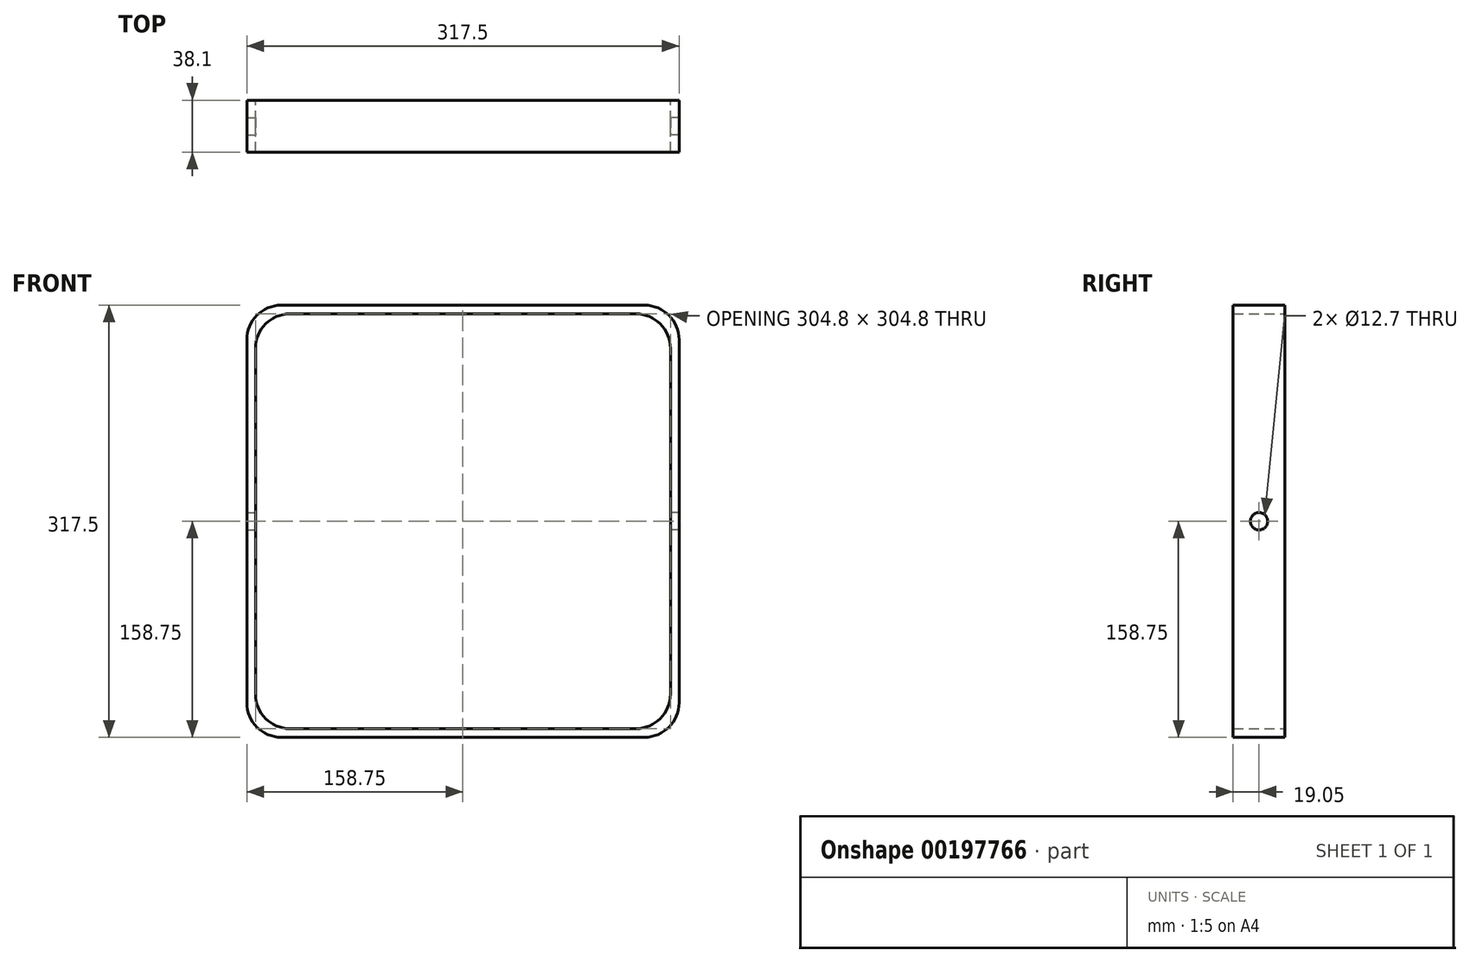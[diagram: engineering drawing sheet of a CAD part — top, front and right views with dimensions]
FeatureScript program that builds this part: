
annotation { "Feature Type Name" : "Feature", "Feature Type Description" : "" }
export const myFeature = defineFeature(function(context is Context, id is Id, definition is map)
    precondition{}
    {
        {
            var Q0;
            Q0=qCreatedBy(makeId("Front.planeOp"),FACE);
            var sketch = newSketch(context, id + "F0", { "sketchPlane" : qUnion([Q0])});
            skLineSegment(sketch, "E0.bottom", {"start": v(152.4, -152.4) * mm, "end": v(-152.4, -152.4) * mm});
            skLineSegment(sketch, "E0.top", {"start": v(152.4, 152.4) * mm, "end": v(-152.4, 152.4) * mm});
            skLineSegment(sketch, "E0.left", {"start": v(152.4, -152.4) * mm, "end": v(152.4, 152.4) * mm});
            skLineSegment(sketch, "E0.right", {"start": v(-152.4, -152.4) * mm, "end": v(-152.4, 152.4) * mm});
            skPoint(sketch, "E0.middle", {"position": v(0, 0) * mm});
            skPoint(sketch, "E1.top.start.orphan", {"position": v(50.8, 44.45) * mm});
            skPoint(sketch, "E1.right.end.orphan", {"position": v(-50.8, 44.45) * mm});
            skPoint(sketch, "E1.bottom.end.orphan", {"position": v(-50.8, -44.45) * mm});
            skPoint(sketch, "E1.bottom.start.orphan", {"position": v(50.8, -44.45) * mm});
            skLineSegment(sketch, "E2.bottom", {"start": v(158.75, -158.75) * mm, "end": v(-158.75, -158.75) * mm});
            skLineSegment(sketch, "E2.top", {"start": v(158.75, 158.75) * mm, "end": v(-158.75, 158.75) * mm});
            skLineSegment(sketch, "E2.left", {"start": v(158.75, -158.75) * mm, "end": v(158.75, 158.75) * mm});
            skLineSegment(sketch, "E2.right", {"start": v(-158.75, -158.75) * mm, "end": v(-158.75, 158.75) * mm});
            skSolve(sketch);
        }
        {
            var Q0;
            Q0=makeQuery(id+"F0.imprint","IMPRINT",FACE,{"disambiguationData":[TD([[makeQuery(id+"F0.imprint","IMPRINT",EDGE,{"derivedFrom":sQuery(id+"F0.wireOp",EDGE,"E0.bottom")}),1.0]])]});
            extrude(context, id + "F1", {"entities" : qUnion([Q0]), "depth" : 38.1 * mm});
        }
        {
            var Q0;
            Q0=makeQuery(id+"F1.opExtrude","SWEPT_EDGE",EDGE,{"disambiguationData":[OSD([sQuery(id+"F0.wireOp",EDGE,"E0.bottom"),sQuery(id+"F0.wireOp",EDGE,"E0.left")])]});
            var Q1;
            Q1=makeQuery(id+"F1.opExtrude","SWEPT_EDGE",EDGE,{"disambiguationData":[OSD([sQuery(id+"F0.wireOp",EDGE,"E0.bottom"),sQuery(id+"F0.wireOp",EDGE,"E0.right")])]});
            var Q2;
            Q2=makeQuery(id+"F1.opExtrude","SWEPT_EDGE",EDGE,{"disambiguationData":[OSD([sQuery(id+"F0.wireOp",EDGE,"E0.top"),sQuery(id+"F0.wireOp",EDGE,"E0.right")])]});
            var Q3;
            Q3=makeQuery(id+"F1.opExtrude","SWEPT_EDGE",EDGE,{"disambiguationData":[OSD([sQuery(id+"F0.wireOp",EDGE,"E0.top"),sQuery(id+"F0.wireOp",EDGE,"E0.left")])]});
            var Q4;
            Q4=makeQuery(id+"F1.opExtrude","SWEPT_EDGE",EDGE,{"disambiguationData":[OSD([sQuery(id+"F0.wireOp",EDGE,"E2.bottom"),sQuery(id+"F0.wireOp",EDGE,"E2.left")])]});
            var Q5;
            Q5=makeQuery(id+"F1.opExtrude","SWEPT_EDGE",EDGE,{"disambiguationData":[OSD([sQuery(id+"F0.wireOp",EDGE,"E2.top"),sQuery(id+"F0.wireOp",EDGE,"E2.left")])]});
            var Q6;
            Q6=makeQuery(id+"F1.opExtrude","SWEPT_EDGE",EDGE,{"disambiguationData":[OSD([sQuery(id+"F0.wireOp",EDGE,"E2.top"),sQuery(id+"F0.wireOp",EDGE,"E2.right")])]});
            var Q7;
            Q7=makeQuery(id+"F1.opExtrude","SWEPT_EDGE",EDGE,{"disambiguationData":[OSD([sQuery(id+"F0.wireOp",EDGE,"E2.bottom"),sQuery(id+"F0.wireOp",EDGE,"E2.right")])]});
            fillet(context, id + "F2", {"entities" : qUnion([Q0, Q1, Q2, Q3, Q4, Q5, Q6, Q7]), "radius" : 25.4 * mm, "tangentPropagation" : true, "allowEdgeOverflow" : false});
        }
        {
            var Q0;
            Q0=qCreatedBy(makeId("Right.planeOp"),FACE);
            var sketch = newSketch(context, id + "F5", { "sketchPlane" : qUnion([Q0])});
            skPoint(sketch, "E3", {"position": v(-19.05, 0) * mm});
            skSolve(sketch);
        }
        {
            var Q0;
            Q0=sQuery(id+"F5.wireOp",VERTEX,"E3");
            var Q1;
            Q1=makeQuery(id+"F1.opExtrude","SWEPT_BODY",BODY,{"disambiguationData":[OSD([sQuery(id+"F0.wireOp",EDGE,"E0.bottom"),sQuery(id+"F0.wireOp",EDGE,"E0.top"),sQuery(id+"F0.wireOp",EDGE,"E0.left"),sQuery(id+"F0.wireOp",EDGE,"E0.right"),sQuery(id+"F0.wireOp",EDGE,"E2.bottom"),sQuery(id+"F0.wireOp",EDGE,"E2.top"),sQuery(id+"F0.wireOp",EDGE,"E2.left"),sQuery(id+"F0.wireOp",EDGE,"E2.right")])]});
            hole(context, id + "F3", {"style" : HoleStyle.SIMPLE, "endStyle" : HoleEndStyle.THROUGH, "holeDiameter" : 12.7 * mm, "locations" : qUnion([Q0]), "scope" : qUnion([Q1]), "isTappedThrough" : true});
        }
        {
            var Q0;
            Q0=sQuery(id+"F5.wireOp",VERTEX,"E3");
            var Q1;
            Q1=makeQuery(id+"F1.opExtrude","SWEPT_BODY",BODY,{"disambiguationData":[OSD([sQuery(id+"F0.wireOp",EDGE,"E0.bottom"),sQuery(id+"F0.wireOp",EDGE,"E0.top"),sQuery(id+"F0.wireOp",EDGE,"E0.left"),sQuery(id+"F0.wireOp",EDGE,"E0.right"),sQuery(id+"F0.wireOp",EDGE,"E2.bottom"),sQuery(id+"F0.wireOp",EDGE,"E2.top"),sQuery(id+"F0.wireOp",EDGE,"E2.left"),sQuery(id+"F0.wireOp",EDGE,"E2.right")])]});
            hole(context, id + "F4", {"style" : HoleStyle.SIMPLE, "endStyle" : HoleEndStyle.THROUGH, "oppositeDirection" : true, "holeDiameter" : 12.7 * mm, "locations" : qUnion([Q0]), "scope" : qUnion([Q1]), "isTappedThrough" : true});
        }
    });
